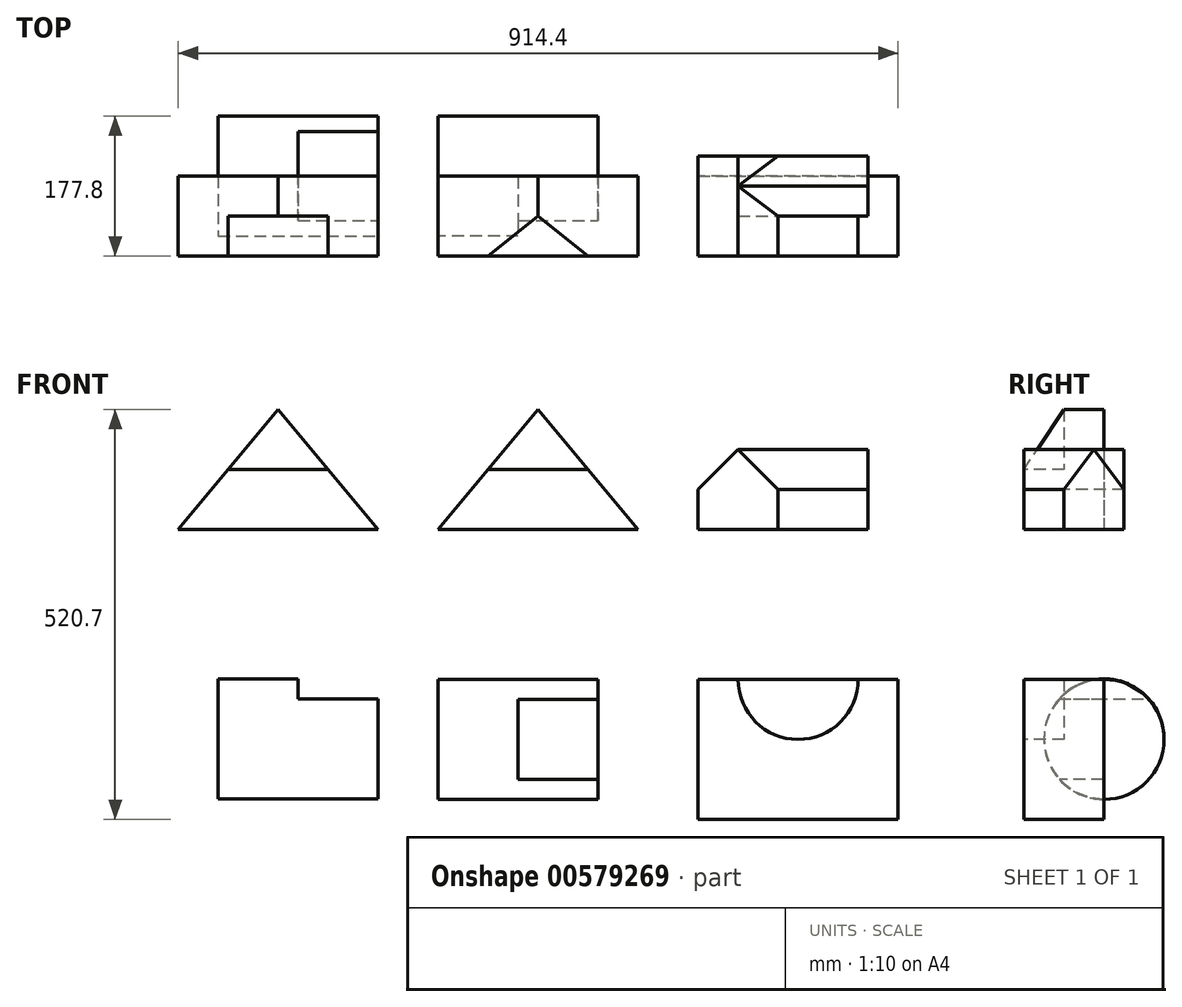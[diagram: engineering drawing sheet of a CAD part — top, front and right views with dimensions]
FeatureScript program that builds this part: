
annotation { "Feature Type Name" : "Feature", "Feature Type Description" : "" }
export const myFeature = defineFeature(function(context is Context, id is Id, definition is map)
    precondition{}
    {
        {
            var Q0;
            Q0=qCreatedBy(makeId("Front.planeOp"),FACE);
            var sketch = newSketch(context, id + "F0", { "sketchPlane" : qUnion([Q0])});
            skLineSegment(sketch, "E0.bottom", {"start": v(0, 0) * mm, "end": v(-254, 0) * mm});
            skLineSegment(sketch, "E1", {"start": v(-127, 152.4) * mm, "end": v(-254, 0) * mm});
            skLineSegment(sketch, "E2", {"start": v(-127, 152.4) * mm, "end": v(0, 0) * mm});
            skLineSegment(sketch, "E3", {"start": v(-127, 76.2) * mm, "end": v(-190.5, 76.2) * mm});
            skLineSegment(sketch, "E4", {"start": v(-127, 76.2) * mm, "end": v(-63.5, 76.2) * mm});
            skPoint(sketch, "E0.right.end.orphan", {"position": v(-254, 152.4) * mm});
            skPoint(sketch, "E0.left.end.orphan", {"position": v(0, 152.4) * mm});
            skSolve(sketch);
        }
        {
            var Q0;
            {var subQ1=sQuery(id+"F0.wireOp",EDGE,"E0.bottom");Q0=makeQuery(id+"F0.imprint","IMPRINT",FACE,{"disambiguationData":[TD([[makeQuery(id+"F0.imprint","IMPRINT",EDGE,{"derivedFrom":subQ1}),-1.0]])]});}
            extrude(context, id + "F1", {"entities" : qUnion([Q0]), "depth" : 50.8 * mm, "offsetDistance" : 25.4 * mm});
        }
        {
            var Q0;
            Q0 = qSketchRegion(id + "F0", true);
            extrude(context, id + "F2", {"entities" : qUnion([Q0]), "operationType" : NewBodyOperationType.ADD, "depth" : 50.8 * mm, "offsetDistance" : 25.4 * mm});
        }
        {
            var Q0;
            {var subQ0=sQuery(id+"F0.wireOp",EDGE,"E2");var subQ1=sQuery(id+"F0.wireOp",EDGE,"E1");var subQ2=sQuery(id+"F0.wireOp",EDGE,"E0.bottom");Q0=makeQuery(id+"F2.boolean.opBoolean","MERGE",FACE,{"derivedFrom":[makeQuery(id+"F1.opExtrude","CAP_FACE",FACE,{"disambiguationData":[OSD([subQ2,subQ1,subQ0,sQuery(id+"F0.wireOp",EDGE,"E3"),sQuery(id+"F0.wireOp",EDGE,"E4")])],"isStart":false}),makeQuery(id+"F2.opExtrude","CAP_FACE",FACE,{"disambiguationData":[OSD([subQ2,subQ1,subQ0])],"isStart":false})]});}
            var sketch = newSketch(context, id + "F3", { "sketchPlane" : qUnion([Q0])});
            skLineSegment(sketch, "E5", {"start": v(-127, 76.2) * mm, "end": v(-190.5, 76.2) * mm});
            skLineSegment(sketch, "E6", {"start": v(-127, 76.2) * mm, "end": v(-63.5, 76.2) * mm});
            skSolve(sketch);
        }
        {
            var Q0;
            Q0 = qSketchRegion(id + "F3", true);
            var Q1;
            {var subQ0=sQuery(id+"F3.wireOp",EDGE,"E5");Q1=makeQuery(id+"F3.imprint","IMPRINT",FACE,{"disambiguationData":[TD([[makeQuery(id+"F3.imprint","IMPRINT",EDGE,{"derivedFrom":subQ0}),-1.0]])]});}
            extrude(context, id + "F4", {"entities" : qUnion([Q0, Q1]), "operationType" : NewBodyOperationType.REMOVE, "oppositeDirection" : true, "depth" : 25.4 * mm, "offsetDistance" : 25.4 * mm});
        }
        {
            var Q0;
            Q0=qCreatedBy(makeId("Front.planeOp"),FACE);
            var sketch = newSketch(context, id + "F5", { "sketchPlane" : qUnion([Q0])});
            skLineSegment(sketch, "E7", {"start": v(76.2, 0) * mm, "end": v(330.2, 0) * mm});
            skLineSegment(sketch, "E8", {"start": v(203.2, 152.4) * mm, "end": v(76.2, 0) * mm});
            skLineSegment(sketch, "E9", {"start": v(203.2, 152.4) * mm, "end": v(330.2, 0) * mm});
            skPoint(sketch, "E10.endSnap0", {"position": v(266.7, 76.2) * mm});
            skSolve(sketch);
        }
        {
            var Q0;
            Q0 = qSketchRegion(id + "F5", true);
            extrude(context, id + "F6", {"entities" : qUnion([Q0]), "depth" : 101.6 * mm, "offsetDistance" : 25.4 * mm});
        }
        {
            var Q0;
            {var subQ0=sQuery(id+"F0.wireOp",EDGE,"E2");var subQ1=sQuery(id+"F0.wireOp",EDGE,"E1");var subQ2=sQuery(id+"F0.wireOp",EDGE,"E0.bottom");Q0=makeQuery(id+"F2.boolean.opBoolean","MERGE",FACE,{"derivedFrom":[makeQuery(id+"F1.opExtrude","CAP_FACE",FACE,{"disambiguationData":[OSD([subQ2,subQ1,subQ0,sQuery(id+"F0.wireOp",EDGE,"E3"),sQuery(id+"F0.wireOp",EDGE,"E4")])],"isStart":false}),makeQuery(id+"F2.opExtrude","CAP_FACE",FACE,{"disambiguationData":[OSD([subQ2,subQ1,subQ0])],"isStart":false})]});}
            extrude(context, id + "F7", {"entities" : qUnion([Q0]), "operationType" : NewBodyOperationType.ADD, "depth" : 50.8 * mm, "offsetDistance" : 25.4 * mm});
        }
        {
            var Q0;
            Q0=makeQuery(id+"F4.boolean.opBoolean","COPY",FACE,{"derivedFrom":makeQuery(id+"F4.opExtrude","CAP_FACE",FACE,{"disambiguationData":[OSD([sQuery(id+"F0.wireOp",EDGE,"E1"),sQuery(id+"F0.wireOp",EDGE,"E2"),sQuery(id+"F3.wireOp",EDGE,"E5"),sQuery(id+"F3.wireOp",EDGE,"E6")])],"isStart":false})});
            extrude(context, id + "F8", {"entities" : qUnion([Q0]), "operationType" : NewBodyOperationType.ADD, "depth" : 25.4 * mm, "offsetDistance" : 25.4 * mm});
        }
        {
            var Q0;
            Q0=makeQuery(id+"F6.opExtrude","CAP_EDGE",EDGE,{"disambiguationData":[OSD([sQuery(id+"F5.wireOp",EDGE,"E7")])],"isStart":false});
            cPoint(context, id + "F9", {"entities" : qUnion([Q0]), "parameter" : 0.5});
        }
        {
            var Q0;
            Q0=makeQuery(id+"F6.opExtrude","CAP_VERTEX",VERTEX,{"disambiguationData":[OSD([sQuery(id+"F5.wireOp",EDGE,"E8"),sQuery(id+"F5.wireOp",EDGE,"E9")])],"isStart":true});
            var Q1;
            Q1=makeQuery(id+"F6.opExtrude","CAP_VERTEX",VERTEX,{"disambiguationData":[OSD([sQuery(id+"F5.wireOp",EDGE,"E8"),sQuery(id+"F5.wireOp",EDGE,"E9")])],"isStart":false});
            var Q2;
            Q2 = qCreatedBy(id + "F9" ,VERTEX);
            cPlane(context, id + "F10", {"entities" : qUnion([Q0, Q1, Q2]), "cplaneType" : CPlaneType.THREE_POINT, "offset" : 25.4 * mm, "width" : 152.4 * mm, "height" : 152.4 * mm});
        }
        {
            var Q0;
            Q0=qCreatedBy(id+"F10.planeOp",FACE);
            var sketch = newSketch(context, id + "F11", { "sketchPlane" : qUnion([Q0])});
            skLineSegment(sketch, "E11.0", {"start": v(101.6, 152.4) * mm, "end": v(0, 152.4) * mm});
            skPoint(sketch, "E12.0", {"position": v(101.6, 152.4) * mm});
            skPoint(sketch, "E13.0", {"position": v(101.6, 0) * mm});
            skLineSegment(sketch, "E14", {"start": v(101.6, 152.4) * mm, "end": v(50.8, 152.4) * mm});
            skLineSegment(sketch, "E15", {"start": v(101.6, 76.2) * mm, "end": v(101.6, 152.4) * mm});
            skLineSegment(sketch, "E16", {"start": v(50.8, 152.4) * mm, "end": v(101.6, 76.2) * mm});
            skSolve(sketch);
        }
        {
            var Q0;
            Q0 = qSketchRegion(id + "F11", true);
            extrude(context, id + "F12", {"entities" : qUnion([Q0]), "operationType" : NewBodyOperationType.REMOVE, "endBound" : BoundingType.SYMMETRIC, "oppositeDirection" : true, "depth" : 127 * mm, "offsetDistance" : 25.4 * mm});
        }
        {
            var Q0;
            Q0=makeQuery(id+"F6.opExtrude","CAP_FACE",FACE,{"disambiguationData":[OSD([sQuery(id+"F5.wireOp",EDGE,"E7"),sQuery(id+"F5.wireOp",EDGE,"E8"),sQuery(id+"F5.wireOp",EDGE,"E9")])],"isStart":false});
            var sketch = newSketch(context, id + "F13", { "sketchPlane" : qUnion([Q0])});
            skLineSegment(sketch, "E17", {"start": v(406.4, 0) * mm, "end": v(406.4, 50.8) * mm});
            skLineSegment(sketch, "E18", {"start": v(406.4, 0) * mm, "end": v(508, 0) * mm});
            skLineSegment(sketch, "E19", {"start": v(508, 0) * mm, "end": v(508, 50.8) * mm});
            skLineSegment(sketch, "E20", {"start": v(406.4, 50.8) * mm, "end": v(457.2, 101.6) * mm});
            skLineSegment(sketch, "E21", {"start": v(508, 50.8) * mm, "end": v(457.2, 101.6) * mm});
            skSolve(sketch);
        }
        {
            var Q0;
            Q0 = qSketchRegion(id + "F13", true);
            extrude(context, id + "F14", {"entities" : qUnion([Q0]), "oppositeDirection" : true, "depth" : 127 * mm, "offsetDistance" : 25.4 * mm});
        }
        {
            var Q0;
            Q0=makeQuery(id+"F14.opExtrude","CAP_EDGE",EDGE,{"disambiguationData":[OSD([sQuery(id+"F13.wireOp",EDGE,"E18")])],"isStart":true});
            cPoint(context, id + "F15", {"entities" : qUnion([Q0]), "parameter" : 0.5});
        }
        {
            var Q0;
            Q0=makeQuery(id+"F14.opExtrude","CAP_VERTEX",VERTEX,{"disambiguationData":[OSD([sQuery(id+"F13.wireOp",EDGE,"E20"),sQuery(id+"F13.wireOp",EDGE,"E21")])],"isStart":true});
            var Q1;
            Q1=makeQuery(id+"F14.opExtrude","CAP_VERTEX",VERTEX,{"disambiguationData":[OSD([sQuery(id+"F13.wireOp",EDGE,"E20"),sQuery(id+"F13.wireOp",EDGE,"E21")])],"isStart":false});
            var Q2;
            Q2 = qCreatedBy(id + "F15" ,VERTEX);
            cPlane(context, id + "F16", {"entities" : qUnion([Q0, Q1, Q2]), "cplaneType" : CPlaneType.THREE_POINT, "offset" : 25.4 * mm, "width" : 152.4 * mm, "height" : 152.4 * mm});
        }
        {
            var Q0;
            Q0=qCreatedBy(id+"F16.planeOp",FACE);
            var sketch = newSketch(context, id + "F17", { "sketchPlane" : qUnion([Q0])});
            skLineSegment(sketch, "E22.0", {"start": v(25.4, 0) * mm, "end": v(25.4, 50.8) * mm});
            skLineSegment(sketch, "E23", {"start": v(25.4, 0) * mm, "end": v(-50.8, 0) * mm});
            skLineSegment(sketch, "E24", {"start": v(-50.8, 0) * mm, "end": v(-50.8, 50.8) * mm});
            skPoint(sketch, "E25.endSnap0", {"position": v(-12.7, 0) * mm});
            skLineSegment(sketch, "E26", {"start": v(-50.8, 50.8) * mm, "end": v(-12.7, 101.6) * mm});
            skLineSegment(sketch, "E27", {"start": v(25.4, 50.8) * mm, "end": v(-12.7, 101.6) * mm});
            skSolve(sketch);
        }
        {
            var Q0;
            Q0 = qSketchRegion(id + "F17", true);
            extrude(context, id + "F18", {"entities" : qUnion([Q0]), "operationType" : NewBodyOperationType.ADD, "depth" : 165.1 * mm, "offsetDistance" : 25.4 * mm});
        }
        {
            var Q0;
            Q0=qCreatedBy(makeId("Right.planeOp"),FACE);
            var sketch = newSketch(context, id + "F19", { "sketchPlane" : qUnion([Q0])});
            skCircle(sketch, "E28", {"center": v(0, -265.82) * mm, "radius": 76.2 * mm});
            skSolve(sketch);
        }
        {
            var Q0;
            Q0=makeQuery(id+"F19.imprint","IMPRINT",FACE,{"disambiguationData":[TD([[makeQuery(id+"F19.imprint","IMPRINT",EDGE,{"derivedFrom":sQuery(id+"F19.wireOp",EDGE,"E28")}),1.0]])]});
            extrude(context, id + "F20", {"entities" : qUnion([Q0]), "oppositeDirection" : true, "depth" : 203.2 * mm, "offsetDistance" : 25.4 * mm});
        }
        {
            var Q0;
            Q0=makeQuery(id+"F20.opExtrude","CAP_FACE",FACE,{"disambiguationData":[OSD([sQuery(id+"F19.wireOp",EDGE,"E28")])],"isStart":true});
            var sketch = newSketch(context, id + "F21", { "sketchPlane" : qUnion([Q0])});
            skLineSegment(sketch, "E29", {"start": v(-56.8, -215.02) * mm, "end": v(56.8, -215.02) * mm});
            skSolve(sketch);
        }
        {
            var Q0;
            Q0 = qSketchRegion(id + "F21", true);
            var Q1;
            {var subQ0=sQuery(id+"F21.wireOp",EDGE,"E29");Q1=makeQuery(id+"F21.imprint","IMPRINT",FACE,{"disambiguationData":[TD([[makeQuery(id+"F21.imprint","IMPRINT",EDGE,{"derivedFrom":subQ0}),1.0]])]});}
            extrude(context, id + "F22", {"entities" : qUnion([Q0, Q1]), "operationType" : NewBodyOperationType.REMOVE, "oppositeDirection" : true, "depth" : 101.6 * mm, "offsetDistance" : 25.4 * mm});
        }
        {
            var Q0;
            Q0=qCreatedBy(makeId("Right.planeOp"),FACE);
            cPlane(context, id + "F23", {"entities" : qUnion([Q0]), "cplaneType" : CPlaneType.OFFSET, "offset" : 76.2 * mm, "width" : 152.4 * mm, "height" : 152.4 * mm});
        }
        {
            var Q0;
            Q0=qCreatedBy(id+"F23.planeOp",FACE);
            var sketch = newSketch(context, id + "F24", { "sketchPlane" : qUnion([Q0])});
            skLineSegment(sketch, "E30.0", {"start": v(-101.6, 0) * mm, "end": v(0, 0) * mm});
            skCircle(sketch, "E31", {"center": v(0, -266.7) * mm, "radius": 76.2 * mm});
            skSolve(sketch);
        }
        {
            var Q0;
            Q0 = qSketchRegion(id + "F24", true);
            extrude(context, id + "F25", {"entities" : qUnion([Q0]), "depth" : 203.2 * mm, "offsetDistance" : 25.4 * mm});
        }
        {
            var Q0;
            Q0=makeQuery(id+"F25.opExtrude","CAP_FACE",FACE,{"disambiguationData":[OSD([sQuery(id+"F24.wireOp",EDGE,"E31")])],"isStart":false});
            var sketch = newSketch(context, id + "F26", { "sketchPlane" : qUnion([Q0])});
            skLineSegment(sketch, "E32", {"start": v(-0.7, -215.9) * mm, "end": v(-56.8, -215.9) * mm});
            skLineSegment(sketch, "E33", {"start": v(-0.7, -215.9) * mm, "end": v(-0.7, -317.5) * mm});
            skLineSegment(sketch, "E34", {"start": v(-0.7, -317.5) * mm, "end": v(-56.8, -317.5) * mm});
            skSolve(sketch);
        }
        {
            var Q0;
            Q0 = qSketchRegion(id + "F26", true);
            var Q1;
            {var subQ0=sQuery(id+"F26.wireOp",EDGE,"E32");Q1=makeQuery(id+"F26.imprint","IMPRINT",FACE,{"disambiguationData":[TD([[makeQuery(id+"F26.imprint","IMPRINT",EDGE,{"derivedFrom":subQ0}),1.0]])]});}
            extrude(context, id + "F27", {"entities" : qUnion([Q0, Q1]), "operationType" : NewBodyOperationType.REMOVE, "oppositeDirection" : true, "depth" : 101.6 * mm, "offsetDistance" : 25.4 * mm});
        }
        {
            var Q0;
            Q0=makeQuery(id+"F14.opExtrude","CAP_FACE",FACE,{"disambiguationData":[OSD([sQuery(id+"F13.wireOp",EDGE,"E17"),sQuery(id+"F13.wireOp",EDGE,"E18"),sQuery(id+"F13.wireOp",EDGE,"E19"),sQuery(id+"F13.wireOp",EDGE,"E20"),sQuery(id+"F13.wireOp",EDGE,"E21")])],"isStart":true});
            var sketch = newSketch(context, id + "F28", { "sketchPlane" : qUnion([Q0])});
            skLineSegment(sketch, "E35", {"start": v(406.4, -190.5) * mm, "end": v(406.4, -368.3) * mm});
            skLineSegment(sketch, "E36", {"start": v(406.4, -368.3) * mm, "end": v(660.4, -368.3) * mm});
            skLineSegment(sketch, "E37", {"start": v(660.4, -368.3) * mm, "end": v(660.4, -190.5) * mm});
            skLineSegment(sketch, "E38", {"start": v(660.4, -190.5) * mm, "end": v(406.4, -190.5) * mm});
            skSolve(sketch);
        }
        {
            var Q0;
            Q0=makeQuery(id+"F28.imprint","IMPRINT",FACE,{"disambiguationData":[TD([[makeQuery(id+"F28.imprint","IMPRINT",EDGE,{"derivedFrom":sQuery(id+"F28.wireOp",EDGE,"E35")}),1.0]])]});
            extrude(context, id + "F29", {"entities" : qUnion([Q0]), "oppositeDirection" : true, "depth" : 101.6 * mm, "offsetDistance" : 25.4 * mm});
        }
        {
            var Q0;
            Q0=makeQuery(id+"F29.opExtrude","CAP_FACE",FACE,{"disambiguationData":[OSD([sQuery(id+"F28.wireOp",EDGE,"E35"),sQuery(id+"F28.wireOp",EDGE,"E36"),sQuery(id+"F28.wireOp",EDGE,"E37"),sQuery(id+"F28.wireOp",EDGE,"E38")])],"isStart":true});
            var sketch = newSketch(context, id + "F30", { "sketchPlane" : qUnion([Q0])});
            skPoint(sketch, "E39.center.orphan", {"position": v(533.4, -190.5) * mm});
            skArc(sketch, "E40", {"start": v(457.2, -190.5) * mm, "mid": v(533.4, -266.7) * mm, "end": v(609.6, -190.5) * mm});
            skSolve(sketch);
        }
        {
            var Q0;
            {var subQ0=sQuery(id+"F30.wireOp",EDGE,"E40");Q0=makeQuery(id+"F30.imprint","IMPRINT",FACE,{"disambiguationData":[TD([[makeQuery(id+"F30.imprint","IMPRINT",EDGE,{"derivedFrom":subQ0}),1.0]])]});}
            extrude(context, id + "F31", {"entities" : qUnion([Q0]), "operationType" : NewBodyOperationType.REMOVE, "oppositeDirection" : true, "depth" : 50.8 * mm, "offsetDistance" : 25.4 * mm});
        }
    });
